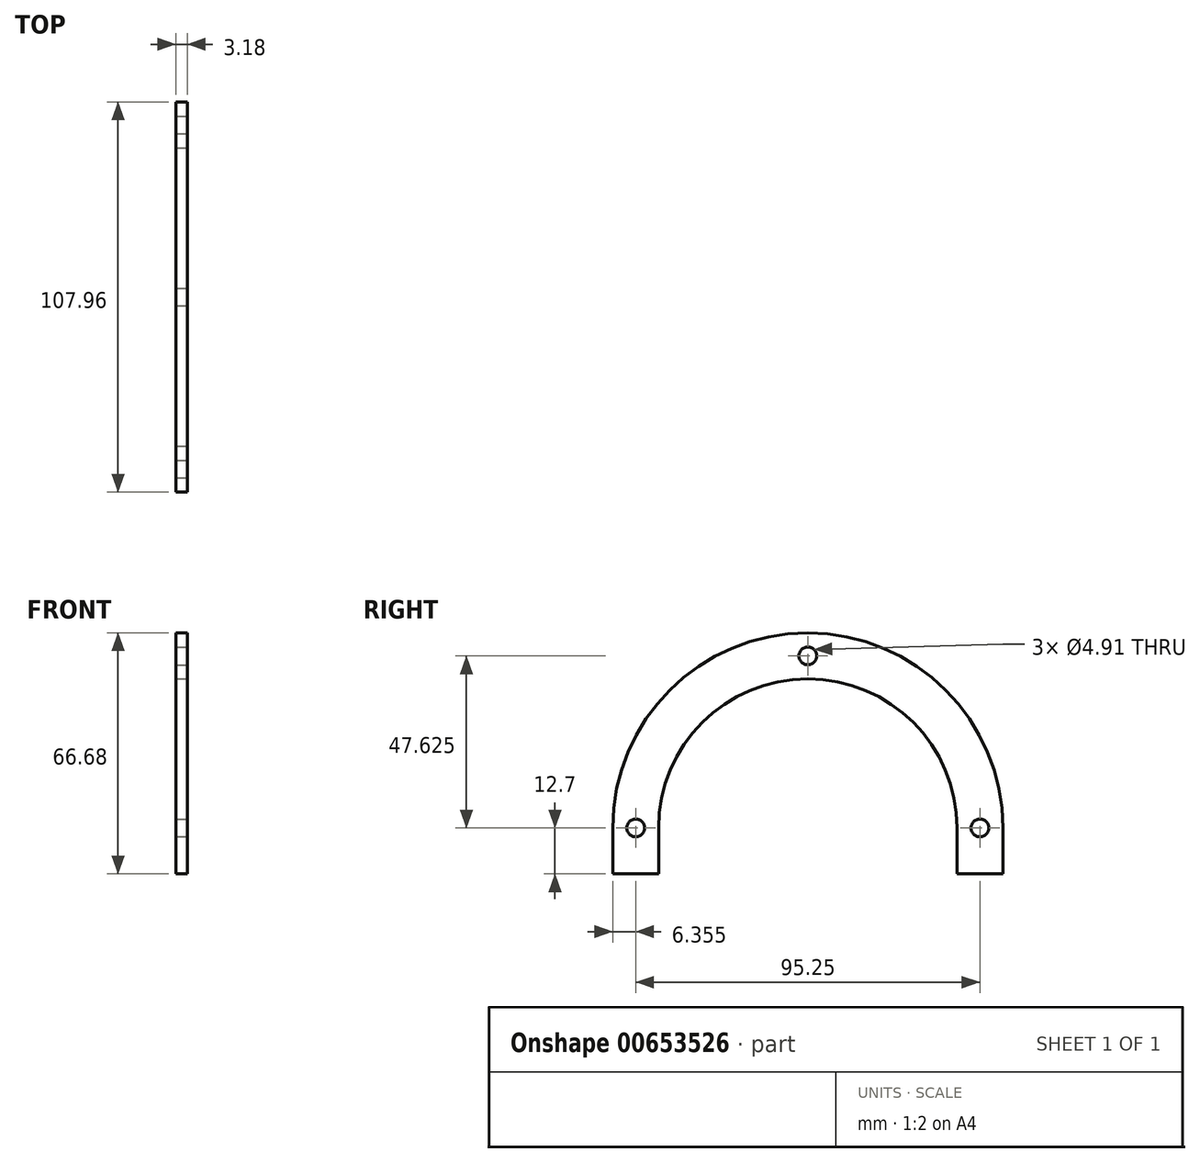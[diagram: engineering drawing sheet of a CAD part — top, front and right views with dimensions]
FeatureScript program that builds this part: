
annotation { "Feature Type Name" : "Feature", "Feature Type Description" : "" }
export const myFeature = defineFeature(function(context is Context, id is Id, definition is map)
    precondition{}
    {
        {
            var Q0;
            Q0=qCreatedBy(makeId("Right.planeOp"),FACE);
            var sketch = newSketch(context, id + "F0", { "sketchPlane" : qUnion([Q0])});
            skArc(sketch, "E0", {"start": v(41.28, 0) * mm, "mid": v(0, 41.28) * mm, "end": v(-41.28, 0) * mm});
            skArc(sketch, "E1", {"start": v(53.98, 0) * mm, "mid": v(0, 53.98) * mm, "end": v(-53.98, 0) * mm});
            skLineSegment(sketch, "E2.0", {"start": v(-41.28, -12.7) * mm, "end": v(-53.98, -12.7) * mm});
            skLineSegment(sketch, "E3", {"start": v(0, 90.21) * mm, "end": v(0, -98.43) * mm, "construction": true});
            skLineSegment(sketch, "E4", {"start": v(-53.98, 0) * mm, "end": v(-53.98, -12.7) * mm});
            skLineSegment(sketch, "E5", {"start": v(-41.28, 0) * mm, "end": v(-41.28, -12.7) * mm});
            skPoint(sketch, "E6.orphan", {"position": v(115.55, 0) * mm});
            skLineSegment(sketch, "E7.MirrorCS", {"start": v(41.28, -12.7) * mm, "end": v(53.98, -12.7) * mm});
            skLineSegment(sketch, "E8.MirrorCS", {"start": v(53.98, 0) * mm, "end": v(53.98, -12.7) * mm});
            skLineSegment(sketch, "E9.MirrorCS", {"start": v(41.28, 0) * mm, "end": v(41.28, -12.7) * mm});
            skCircle(sketch, "E10", {"center": v(0, 0) * mm, "radius": 47.63 * mm, "construction": true});
            skPoint(sketch, "E11", {"position": v(0, 47.63) * mm});
            skPoint(sketch, "E12.1.0", {"position": v(-47.63, 0) * mm});
            skPoint(sketch, "E12.3.0", {"position": v(47.63, 0) * mm});
            skSolve(sketch);
        }
        {
            var Q0;
            Q0 = qSketchRegion(id + "F0", true);
            extrude(context, id + "F1", {"entities" : qUnion([Q0]), "oppositeDirection" : true, "depth" : 3.17 * mm, "offsetDistance" : 25.4 * mm});
        }
        {
            var Q0;
            Q0=sQuery(id+"F0.wireOp",VERTEX,"E12.1.0");
            var Q1;
            Q1=sQuery(id+"F0.wireOp",VERTEX,"E11");
            var Q2;
            Q2=sQuery(id+"F0.wireOp",VERTEX,"E12.3.0");
            var Q3;
            Q3=makeQuery(id+"F1.opExtrude","SWEPT_BODY",BODY,{"disambiguationData":[OSD([sQuery(id+"F0.wireOp",EDGE,"E0"),sQuery(id+"F0.wireOp",EDGE,"E1"),sQuery(id+"F0.wireOp",EDGE,"E2.0"),sQuery(id+"F0.wireOp",EDGE,"E4"),sQuery(id+"F0.wireOp",EDGE,"E5"),sQuery(id+"F0.wireOp",EDGE,"E7.MirrorCS"),sQuery(id+"F0.wireOp",EDGE,"E8.MirrorCS"),sQuery(id+"F0.wireOp",EDGE,"E9.MirrorCS")])]});
            hole(context, id + "F2", {"style" : HoleStyle.SIMPLE, "endStyle" : HoleEndStyle.THROUGH, "standardTappedOrClearance" : lookupTablePath({ "standard" : "ANSI", "size" : "#10 (0.2)", "type" : "Drilled" }), "standardBlindInLast" : lookupTablePath({ "standard" : "ANSI", "size" : "#10", "type" : "Drilled" }), "holeDiameter" : 4.9 * mm, "majorDiameter" : 6.35 * mm, "isTappedThrough" : true, "tappedDepth" : 7.95 * mm, "tapClearance" : 3, "startFromSketch" : true, "locations" : qUnion([Q0, Q1, Q2]), "scope" : qUnion([Q3])});
        }
    });
